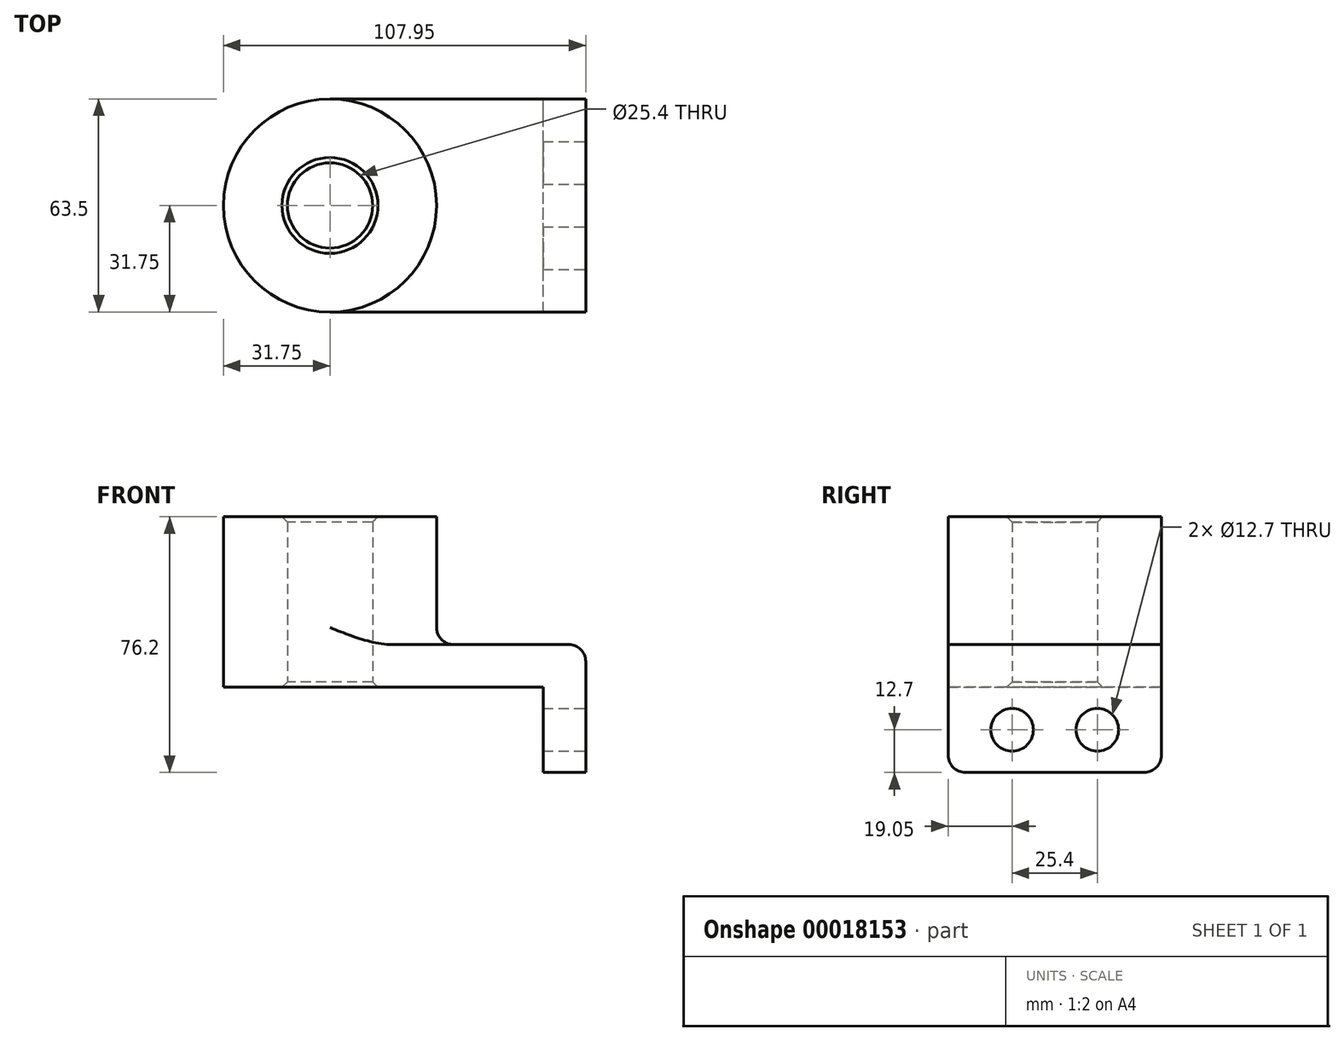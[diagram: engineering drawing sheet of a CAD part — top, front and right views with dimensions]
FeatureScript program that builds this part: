
annotation { "Feature Type Name" : "Feature", "Feature Type Description" : "" }
export const myFeature = defineFeature(function(context is Context, id is Id, definition is map)
    precondition{}
    {
        {
            var Q0;
            Q0=qCreatedBy(makeId("Top.planeOp"),FACE);
            var sketch = newSketch(context, id + "F0", { "sketchPlane" : qUnion([Q0])});
            skLineSegment(sketch, "E0.rect.bottom", {"start": v(38.1, 31.75) * mm, "end": v(-38.1, 31.75) * mm});
            skLineSegment(sketch, "E0.rect.top", {"start": v(38.1, -31.75) * mm, "end": v(-38.1, -31.75) * mm});
            skLineSegment(sketch, "E0.rect.left", {"start": v(38.1, 31.75) * mm, "end": v(38.1, -31.75) * mm});
            skLineSegment(sketch, "E0.rect.right", {"start": v(-38.1, 31.75) * mm, "end": v(-38.1, -31.75) * mm});
            skPoint(sketch, "E0.rect.middle", {"position": v(0, 0) * mm});
            skCircle(sketch, "E1", {"center": v(-38.1, 0) * mm, "radius": 31.75 * mm});
            skCircle(sketch, "E2", {"center": v(-38.1, 0) * mm, "radius": 12.7 * mm});
            skSolve(sketch);
        }
        {
            var Q0;
            Q0 = qSketchRegion(id + "F0", true);
            extrude(context, id + "F1", {"entities" : qUnion([Q0]), "depth" : 12.7 * mm});
        }
        {
            var Q0;
            {var subQ0=sQuery(id+"F0.wireOp",EDGE,"E2");var subQ1=sQuery(id+"F0.wireOp",EDGE,"E0.rect.right");var subQ3=makeQuery(id+"F0.imprint","INTERSECT",VERTEX,{"disambiguationData":[OD(0.0)],"derivedFrom":[subQ1,subQ0]});Q0=makeQuery(id+"F0.imprint","IMPRINT",FACE,{"disambiguationData":[TD([[makeQuery(id+"F0.imprint","IMPRINT",EDGE,{"disambiguationData":[TD([[subQ3,-1.0]])],"derivedFrom":subQ0}),-1.0]])]});}
            var Q1;
            {var subQ0=sQuery(id+"F0.wireOp",EDGE,"E2");var subQ1=sQuery(id+"F0.wireOp",EDGE,"E0.rect.right");var subQ3=makeQuery(id+"F0.imprint","INTERSECT",VERTEX,{"disambiguationData":[OD(0.0)],"derivedFrom":[subQ1,subQ0]});Q1=makeQuery(id+"F0.imprint","IMPRINT",FACE,{"disambiguationData":[TD([[makeQuery(id+"F0.imprint","IMPRINT",EDGE,{"disambiguationData":[TD([[subQ3,1.0]])],"derivedFrom":subQ0}),-1.0]])]});}
            extrude(context, id + "F2", {"entities" : qUnion([Q0, Q1]), "operationType" : NewBodyOperationType.ADD, "depth" : 50.8 * mm});
        }
        {
            var Q0;
            Q0=makeQuery(id+"F1.opExtrude","SWEPT_FACE",FACE,{"disambiguationData":[OSD([sQuery(id+"F0.wireOp",EDGE,"E0.rect.left")])]});
            var sketch = newSketch(context, id + "F3", { "sketchPlane" : qUnion([Q0])});
            skLineSegment(sketch, "E3.bottom", {"start": v(-31.75, 12.7) * mm, "end": v(31.75, 12.7) * mm});
            skLineSegment(sketch, "E3.top", {"start": v(-31.75, -25.4) * mm, "end": v(31.75, -25.4) * mm});
            skLineSegment(sketch, "E3.left", {"start": v(-31.75, 12.7) * mm, "end": v(-31.75, -25.4) * mm});
            skLineSegment(sketch, "E3.right", {"start": v(31.75, 12.7) * mm, "end": v(31.75, -25.4) * mm});
            skCircle(sketch, "E4", {"center": v(-12.7, -12.7) * mm, "radius": 6.35 * mm});
            skLineSegment(sketch, "E5", {"start": v(0, -3.02) * mm, "end": v(0, -25.4) * mm, "construction": true});
            skCircle(sketch, "E6.MirrorC", {"center": v(12.7, -12.7) * mm, "radius": 6.35 * mm});
            skSolve(sketch);
        }
        {
            var Q0;
            Q0 = qSketchRegion(id + "F3", true);
            extrude(context, id + "F4", {"entities" : qUnion([Q0]), "operationType" : NewBodyOperationType.ADD, "oppositeDirection" : true, "depth" : 12.7 * mm});
        }
        {
            var Q0;
            {var subQ0=sQuery(id+"F0.wireOp",EDGE,"E1");Q0=makeQuery(id+"F2.boolean.opBoolean","INTERSECT",EDGE,{"derivedFrom":[makeQuery(id+"F1.opExtrude","CAP_FACE",FACE,{"disambiguationData":[OSD([sQuery(id+"F0.wireOp",EDGE,"E0.rect.bottom"),sQuery(id+"F0.wireOp",EDGE,"E0.rect.top"),sQuery(id+"F0.wireOp",EDGE,"E0.rect.left"),subQ0,sQuery(id+"F0.wireOp",EDGE,"E2")])],"isStart":false}),makeQuery(id+"F2.opExtrude","SWEPT_FACE",FACE,{"disambiguationData":[OSD([subQ0])]})]});}
            var Q1;
            Q1=makeQuery(id+"F1.opExtrude","CAP_EDGE",EDGE,{"disambiguationData":[OSD([sQuery(id+"F0.wireOp",EDGE,"E0.rect.left")])],"isStart":false});
            var Q2;
            Q2=makeQuery(id+"F4.opExtrude","SWEPT_EDGE",EDGE,{"disambiguationData":[OSD([sQuery(id+"F3.wireOp",EDGE,"E3.top"),sQuery(id+"F3.wireOp",EDGE,"E3.left")])]});
            var Q3;
            Q3=makeQuery(id+"F4.opExtrude","SWEPT_EDGE",EDGE,{"disambiguationData":[OSD([sQuery(id+"F3.wireOp",EDGE,"E3.top"),sQuery(id+"F3.wireOp",EDGE,"E3.right")])]});
            fillet(context, id + "F5", {"entities" : qUnion([Q0, Q1, Q2, Q3]), "radius" : 5.08 * mm, "tangentPropagation" : true, "allowEdgeOverflow" : false});
        }
        {
            var Q0;
            {var subQ0=sQuery(id+"F0.wireOp",EDGE,"E2");Q0=makeQuery(id+"F2.boolean.opBoolean","MERGE",FACE,{"derivedFrom":[makeQuery(id+"F1.opExtrude","SWEPT_FACE",FACE,{"disambiguationData":[OSD([subQ0])]}),makeQuery(id+"F2.opExtrude","SWEPT_FACE",FACE,{"disambiguationData":[OSD([subQ0])]})]});}
            chamfer(context, id + "F6", {"entities" : qUnion([Q0]), "width" : 1.59 * mm, "tangentPropagation" : true});
        }
    });
